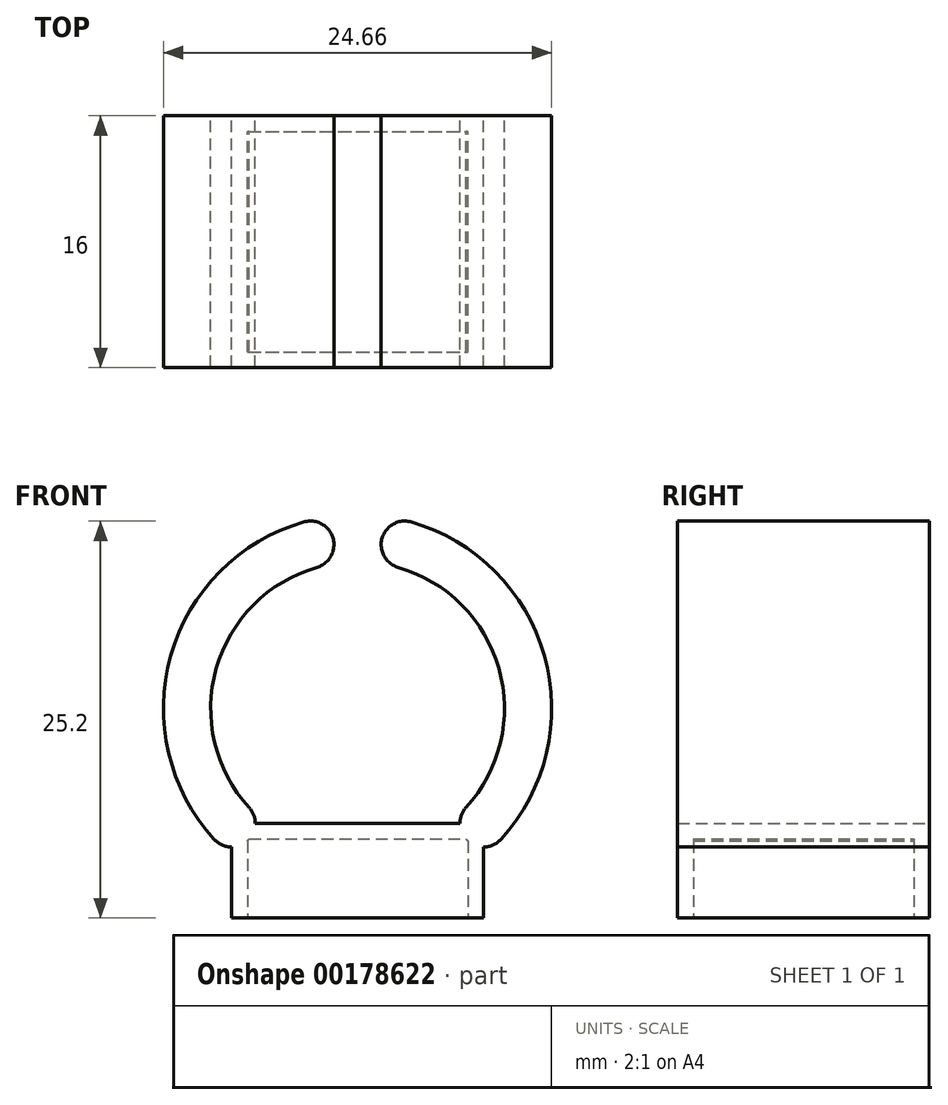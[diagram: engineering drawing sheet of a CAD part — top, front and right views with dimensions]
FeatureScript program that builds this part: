
annotation { "Feature Type Name" : "Feature", "Feature Type Description" : "" }
export const myFeature = defineFeature(function(context is Context, id is Id, definition is map)
    precondition{}
    {
        {
            var Q0;
            Q0=qCreatedBy(makeId("Top.planeOp"),FACE);
            var sketch = newSketch(context, id + "F0", { "sketchPlane" : qUnion([Q0])});
            skLineSegment(sketch, "E0.bottom", {"start": v(0, 0) * mm, "end": v(16, 0) * mm});
            skLineSegment(sketch, "E0.top", {"start": v(0, -16) * mm, "end": v(16, -16) * mm});
            skLineSegment(sketch, "E0.left", {"start": v(0, 0) * mm, "end": v(0, -16) * mm});
            skLineSegment(sketch, "E0.right", {"start": v(16, 0) * mm, "end": v(16, -16) * mm});
            skSolve(sketch);
        }
        {
            var Q0;
            Q0 = qSketchRegion(id + "F0", true);
            extrude(context, id + "F1", {"entities" : qUnion([Q0]), "depth" : 6 * mm});
        }
        {
            var Q0;
            Q0=makeQuery(id+"F1.opExtrude","CAP_FACE",FACE,{"disambiguationData":[OSD([sQuery(id+"F0.wireOp",EDGE,"E0.bottom"),sQuery(id+"F0.wireOp",EDGE,"E0.top"),sQuery(id+"F0.wireOp",EDGE,"E0.left"),sQuery(id+"F0.wireOp",EDGE,"E0.right")])],"isStart":true});
            shell(context, id + "F2", {"entities" : qUnion([Q0]), "thickness" : 1 * mm});
        }
        {
            var Q0;
            Q0=qCreatedBy(makeId("Front.planeOp"),FACE);
            var sketch = newSketch(context, id + "F3", { "sketchPlane" : qUnion([Q0])});
            skLineSegment(sketch, "E1", {"start": v(8, 6) * mm, "end": v(8, 20.6) * mm, "construction": true});
            skArc(sketch, "E2", {"start": v(16, 6) * mm, "mid": v(18.42, 16.24) * mm, "end": v(11, 23.7) * mm});
            skArc(sketch, "E3.0.startCap", {"start": v(17.1, 4.99) * mm, "mid": v(14.99, 4.9) * mm, "end": v(14.9, 7.01) * mm});
            skArc(sketch, "E3.0.endCap", {"start": v(10.58, 22.26) * mm, "mid": v(9.56, 24.12) * mm, "end": v(11.42, 25.14) * mm});
            skArc(sketch, "E3.0.left", {"start": v(14.9, 7.01) * mm, "mid": v(16.98, 15.83) * mm, "end": v(10.58, 22.26) * mm});
            skArc(sketch, "E3.0.right", {"start": v(17.1, 4.99) * mm, "mid": v(19.86, 16.65) * mm, "end": v(11.42, 25.14) * mm});
            skArc(sketch, "E4.MirrorCS", {"start": v(-1.1, 4.99) * mm, "mid": v(-3.86, 16.65) * mm, "end": v(4.58, 25.14) * mm});
            skArc(sketch, "E5.MirrorCS", {"start": v(1.1, 7.01) * mm, "mid": v(-0.98, 15.83) * mm, "end": v(5.42, 22.26) * mm});
            skArc(sketch, "E6.MirrorCS", {"start": v(5.42, 22.26) * mm, "mid": v(6.44, 24.12) * mm, "end": v(4.58, 25.14) * mm});
            skArc(sketch, "E7.MirrorCS", {"start": v(-1.1, 4.99) * mm, "mid": v(1.01, 4.9) * mm, "end": v(1.1, 7.01) * mm});
            skArc(sketch, "E8.MirrorCS", {"start": v(0, 6) * mm, "mid": v(-2.42, 16.24) * mm, "end": v(5, 23.7) * mm});
            skSolve(sketch);
        }
        {
            var Q0;
            Q0 = qSketchRegion(id + "F3", true);
            extrude(context, id + "F4", {"entities" : qUnion([Q0]), "operationType" : NewBodyOperationType.ADD, "depth" : 16 * mm});
        }
    });
